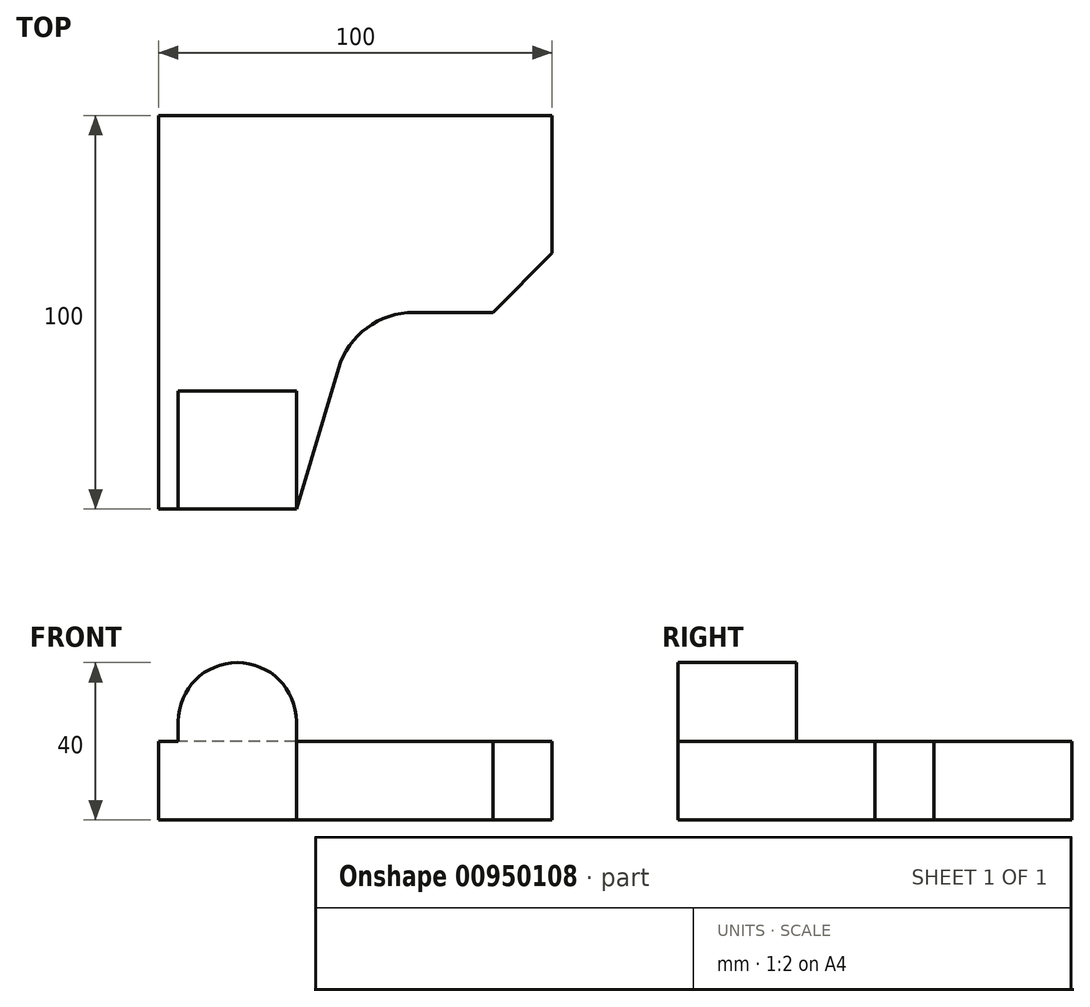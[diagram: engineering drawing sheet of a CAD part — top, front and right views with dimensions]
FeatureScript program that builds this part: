
annotation { "Feature Type Name" : "Feature", "Feature Type Description" : "" }
export const myFeature = defineFeature(function(context is Context, id is Id, definition is map)
    precondition{}
    {
        {
            var Q0;
            Q0=qCreatedBy(makeId("Top.planeOp"),FACE);
            var sketch = newSketch(context, id + "F0", { "sketchPlane" : qUnion([Q0])});
            skLineSegment(sketch, "E0", {"start": v(0, 0) * mm, "end": v(0, 100) * mm});
            skLineSegment(sketch, "E1", {"start": v(0, 100) * mm, "end": v(100, 100) * mm});
            skLineSegment(sketch, "E2", {"start": v(100, 100) * mm, "end": v(100, 65) * mm});
            skLineSegment(sketch, "E3", {"start": v(100, 65) * mm, "end": v(85, 50) * mm});
            skLineSegment(sketch, "E4", {"start": v(85, 50) * mm, "end": v(50, 50) * mm});
            skLineSegment(sketch, "E5", {"start": v(50, 50) * mm, "end": v(35, 0) * mm});
            skLineSegment(sketch, "E6", {"start": v(35, 0) * mm, "end": v(0, 0) * mm});
            skSolve(sketch);
        }
        {
            var Q0;
            Q0 = qSketchRegion(id + "F0", true);
            extrude(context, id + "F1", {"entities" : qUnion([Q0]), "depth" : 20 * mm, "offsetDistance" : 25 * mm});
        }
        {
            var Q0;
            Q0=makeQuery(id+"F1.opExtrude","SWEPT_EDGE",EDGE,{"disambiguationData":[OSD([sQuery(id+"F0.wireOp",EDGE,"E4"),sQuery(id+"F0.wireOp",EDGE,"E5")])]});
            fillet(context, id + "F2", {"entities" : qUnion([Q0]), "radius" : 20 * mm, "tangentPropagation" : true, "allowEdgeOverflow" : false});
        }
        {
            var Q0;
            Q0=makeQuery(id+"F1.opExtrude","SWEPT_FACE",FACE,{"disambiguationData":[OSD([sQuery(id+"F0.wireOp",EDGE,"E6")])]});
            var sketch = newSketch(context, id + "F3", { "sketchPlane" : qUnion([Q0])});
            skArc(sketch, "E7", {"start": v(35, 25) * mm, "mid": v(20, 40) * mm, "end": v(5, 25) * mm});
            skLineSegment(sketch, "E8", {"start": v(35, 25) * mm, "end": v(35, 20) * mm});
            skLineSegment(sketch, "E9", {"start": v(35, 20) * mm, "end": v(5, 20) * mm});
            skLineSegment(sketch, "E10", {"start": v(5, 20) * mm, "end": v(5, 25) * mm});
            skSolve(sketch);
        }
        {
            var Q0;
            Q0 = qSketchRegion(id + "F3", true);
            extrude(context, id + "F4", {"entities" : qUnion([Q0]), "operationType" : NewBodyOperationType.ADD, "oppositeDirection" : true, "depth" : 30 * mm, "offsetDistance" : 25 * mm});
        }
    });
